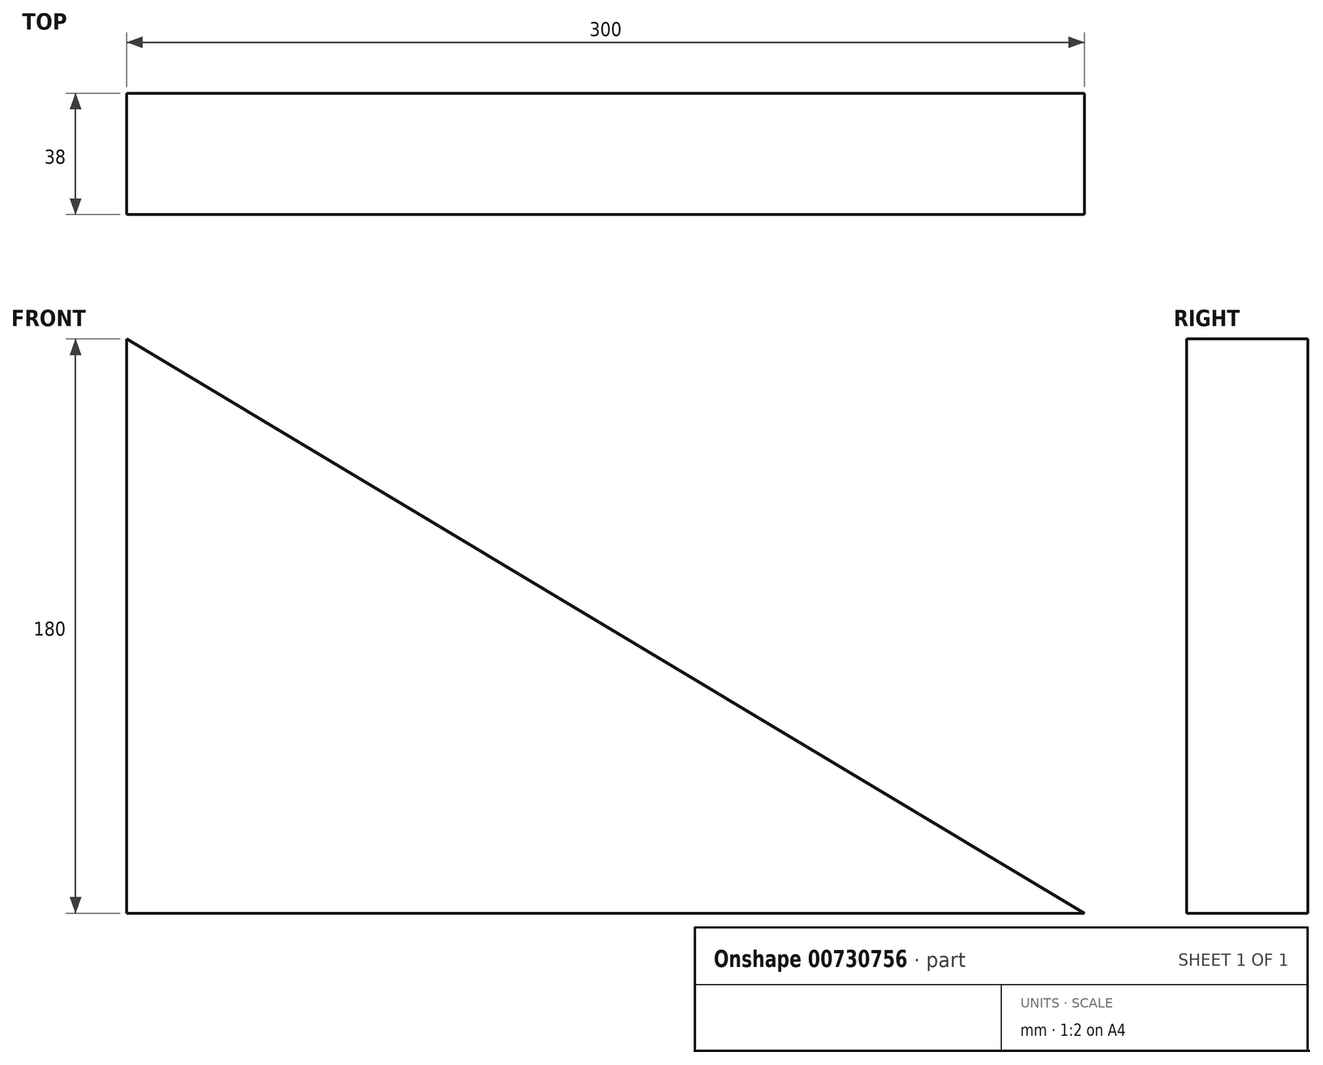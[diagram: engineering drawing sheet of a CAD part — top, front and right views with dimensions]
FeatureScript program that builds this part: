
annotation { "Feature Type Name" : "Feature", "Feature Type Description" : "" }
export const myFeature = defineFeature(function(context is Context, id is Id, definition is map)
    precondition{}
    {
        {
            var Q0;
            Q0=qCreatedBy(makeId("Front.planeOp"),FACE);
            var sketch = newSketch(context, id + "F0", { "sketchPlane" : qUnion([Q0])});
            skLineSegment(sketch, "E0", {"start": v(-175.44, 120.65) * mm, "end": v(-175.44, -59.35) * mm});
            skLineSegment(sketch, "E1", {"start": v(-175.44, -59.35) * mm, "end": v(124.56, -59.35) * mm});
            skLineSegment(sketch, "E2", {"start": v(124.56, -59.35) * mm, "end": v(-175.44, 120.65) * mm});
            skSolve(sketch);
        }
        {
            var Q0;
            Q0 = qSketchRegion(id + "F0", true);
            extrude(context, id + "F1", {"entities" : qUnion([Q0]), "endBound" : BoundingType.SYMMETRIC, "depth" : 38 * mm, "offsetDistance" : 25.4 * mm});
        }
    });
